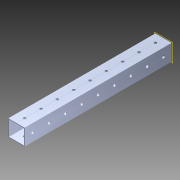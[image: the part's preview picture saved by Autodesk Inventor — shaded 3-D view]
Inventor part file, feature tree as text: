
AUTODESK INVENTOR PART (.ipt)
format: ipt  version: 2014 SP1 (Build 180222100, 222)  size: 1,157,120 bytes
history: native  units: in
note: dims shown in document units (in); Inventor stores cm internally (conversion verified against a paired STEP export)
features: pattern_circular x1, other x1, plane x1, extrude x1, imported_body x1, sketch x1
ambient origin geometry x8: Origin, YZ Plane, XZ Plane, XY Plane, X Axis, Y Axis, Z Axis, Center Point
bodies: Body1 (feature_tree)
feature tree (6):
  pattern_circular  "CirPattern2"
  other  "217-3426-STEP1"
  plane  "Work Plane1"
  extrude  "Extrusion1"  Depth=3937.0079in TaperAngle=0.0deg
  imported_body  "Base1"
  sketch  "Sketch1"  dims[d0=-9.0in d1=3937.0079in d2=0.0in]
